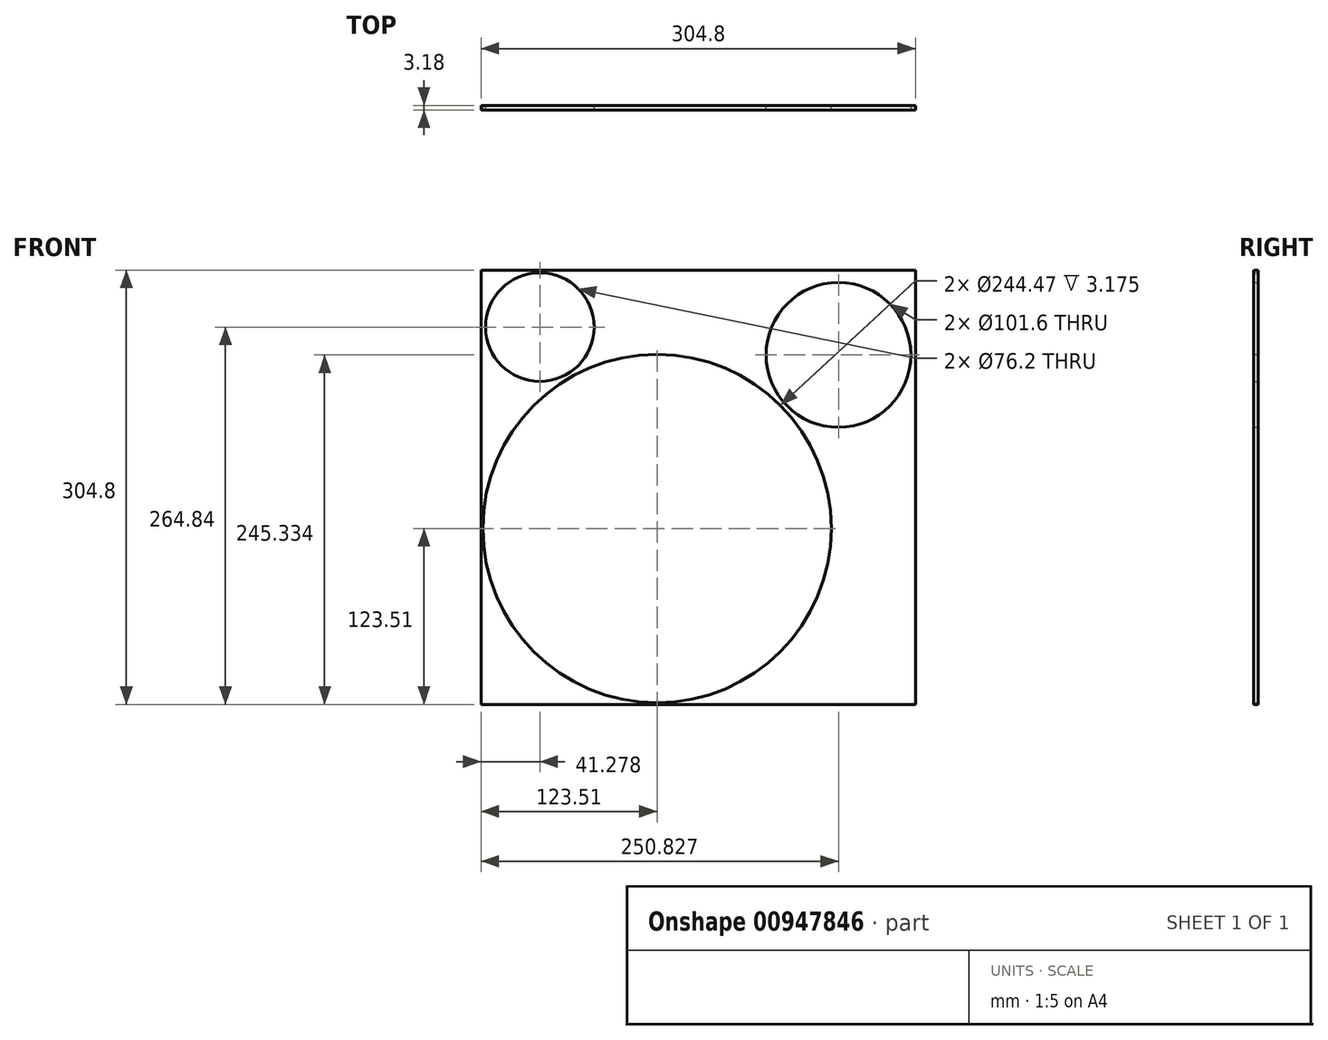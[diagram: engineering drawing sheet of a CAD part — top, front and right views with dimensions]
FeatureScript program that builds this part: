
annotation { "Feature Type Name" : "Feature", "Feature Type Description" : "" }
export const myFeature = defineFeature(function(context is Context, id is Id, definition is map)
    precondition{}
    {
        {
            var Q0;
            Q0=qCreatedBy(makeId("Front.planeOp"),FACE);
            var sketch = newSketch(context, id + "F0", { "sketchPlane" : qUnion([Q0])});
            skCircle(sketch, "E0", {"center": v(0, 0) * mm, "radius": 122.24 * mm});
            skLineSegment(sketch, "E1.bottom", {"start": v(-123.5, 181.3) * mm, "end": v(181.3, 181.3) * mm});
            skLineSegment(sketch, "E1.top", {"start": v(-123.5, -123.5) * mm, "end": v(181.3, -123.5) * mm});
            skLineSegment(sketch, "E1.left", {"start": v(-123.5, 181.3) * mm, "end": v(-123.5, -123.5) * mm});
            skLineSegment(sketch, "E1.right", {"start": v(181.3, 181.3) * mm, "end": v(181.3, -123.5) * mm});
            skCircle(sketch, "E2", {"center": v(127.32, 121.82) * mm, "radius": 50.8 * mm});
            skCircle(sketch, "E3", {"center": v(-82.23, 141.33) * mm, "radius": 38.1 * mm});
            skSolve(sketch);
        }
        {
            var Q0;
            Q0 = qSketchRegion(id + "F0", true);
            extrude(context, id + "F1", {"entities" : qUnion([Q0]), "depth" : 3.17 * mm, "offsetDistance" : 25.4 * mm});
        }
    });
